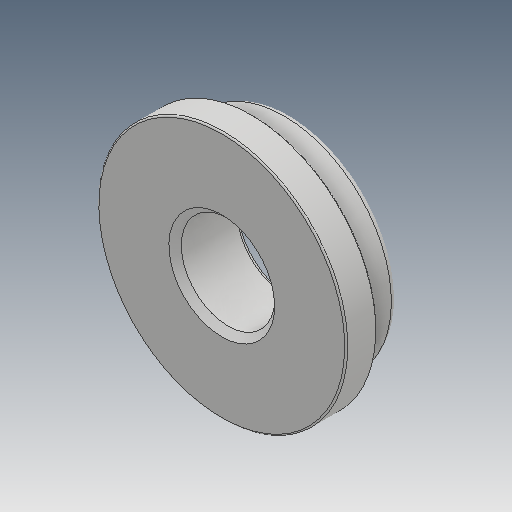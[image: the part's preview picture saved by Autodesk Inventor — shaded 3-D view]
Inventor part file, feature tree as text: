
AUTODESK INVENTOR PART (.ipt)
format: ipt  version: 2018 (Build 220112000, 112)  size: 183,808 bytes
history: native  units: mm
features: fillet x1
ambient origin geometry x8: Origin, YZ Plane, XZ Plane, XY Plane, X Axis, Y Axis, Z Axis, Center Point
bodies: Volumenkörper1 (feature_tree)
feature tree (1):
  fillet  "Fillet3"  [1 undecoded]
note: 1 required parameter value undecoded (feature->parameter linkage not recoverable at this tier; creation-order binding heuristic only, values carry confidence <= 0.55)
